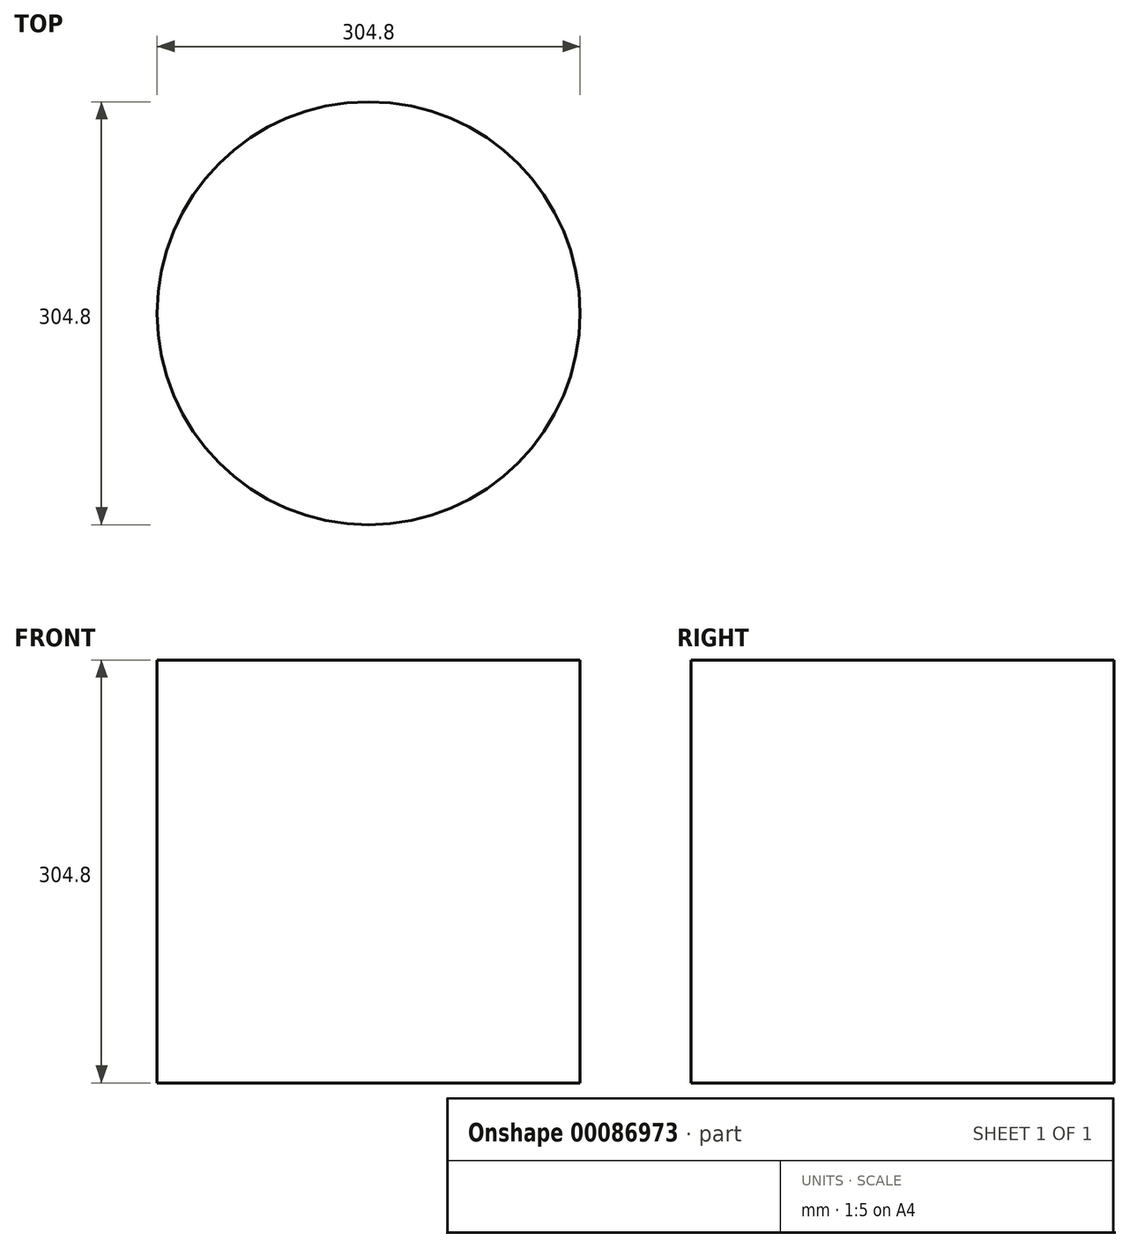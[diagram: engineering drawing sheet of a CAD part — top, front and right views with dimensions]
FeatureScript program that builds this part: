
annotation { "Feature Type Name" : "Feature", "Feature Type Description" : "" }
export const myFeature = defineFeature(function(context is Context, id is Id, definition is map)
    precondition{}
    {
        {
            var Q0;
            Q0=qCreatedBy(makeId("Top.planeOp"),FACE);
            var sketch = newSketch(context, id + "F0", { "sketchPlane" : qUnion([Q0])});
            skCircle(sketch, "E0", {"center": v(0, 0) * mm, "radius": 152.4 * mm});
            skSolve(sketch);
        }
        {
            var Q0;
            Q0=makeQuery(id+"F0.imprint","IMPRINT",FACE,{"disambiguationData":[TD([[makeQuery(id+"F0.imprint","IMPRINT",EDGE,{"derivedFrom":sQuery(id+"F0.wireOp",EDGE,"E0")}),1.0]])]});
            extrude(context, id + "F1", {"entities" : qUnion([Q0]), "depth" : 304.8 * mm});
        }
    });
